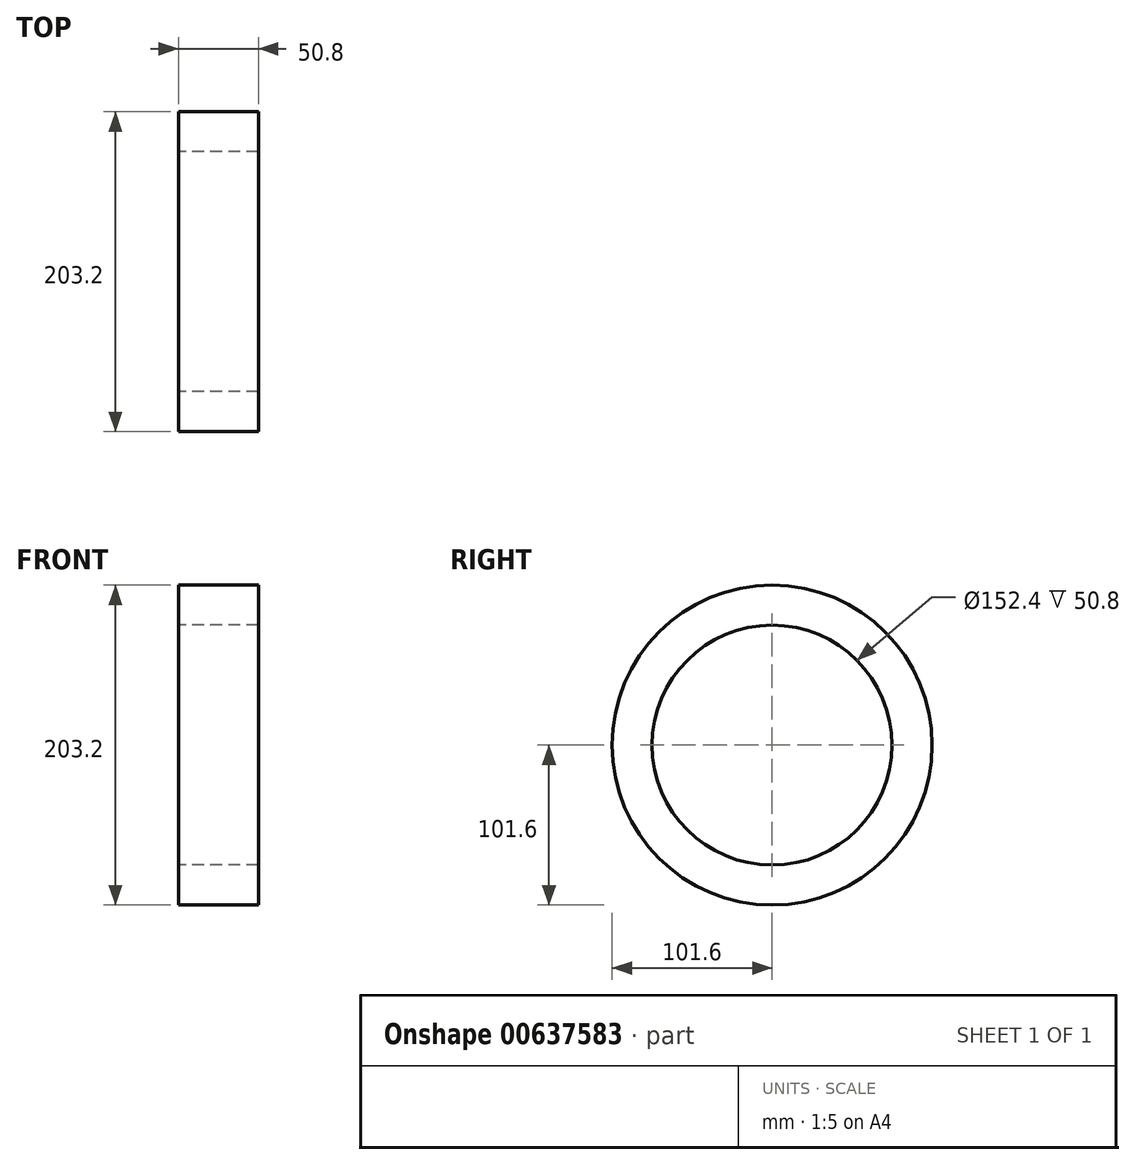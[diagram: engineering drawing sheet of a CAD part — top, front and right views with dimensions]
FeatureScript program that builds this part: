
annotation { "Feature Type Name" : "Feature", "Feature Type Description" : "" }
export const myFeature = defineFeature(function(context is Context, id is Id, definition is map)
    precondition{}
    {
        {
            var Q0;
            Q0=qCreatedBy(makeId("Top.planeOp"),FACE);
            var sketch = newSketch(context, id + "F0", { "sketchPlane" : qUnion([Q0])});
            skLineSegment(sketch, "E0.bottom", {"start": v(0, 76.2) * mm, "end": v(50.8, 76.2) * mm});
            skLineSegment(sketch, "E0.top", {"start": v(0, 101.6) * mm, "end": v(50.8, 101.6) * mm});
            skLineSegment(sketch, "E0.left", {"start": v(0, 76.2) * mm, "end": v(0, 101.6) * mm});
            skLineSegment(sketch, "E0.right", {"start": v(50.8, 76.2) * mm, "end": v(50.8, 101.6) * mm});
            skLineSegment(sketch, "E1", {"start": v(0, 0) * mm, "end": v(77.46, 0) * mm, "construction": true});
            skSolve(sketch);
        }
        {
            var Q0;
            Q0=makeQuery(id+"F0.imprint","IMPRINT",FACE,{"disambiguationData":[TD([[makeQuery(id+"F0.imprint","IMPRINT",EDGE,{"derivedFrom":sQuery(id+"F0.wireOp",EDGE,"E0.bottom")}),1.0]])]});
            var Q1;
            Q1=sQuery(id+"F0.wireOp",EDGE,"E1");
            revolve(context, id + "F1", {"entities" : qUnion([Q0]), "axis" : qUnion([Q1]), "revolveType" : RevolveType.FULL});
        }
    });
